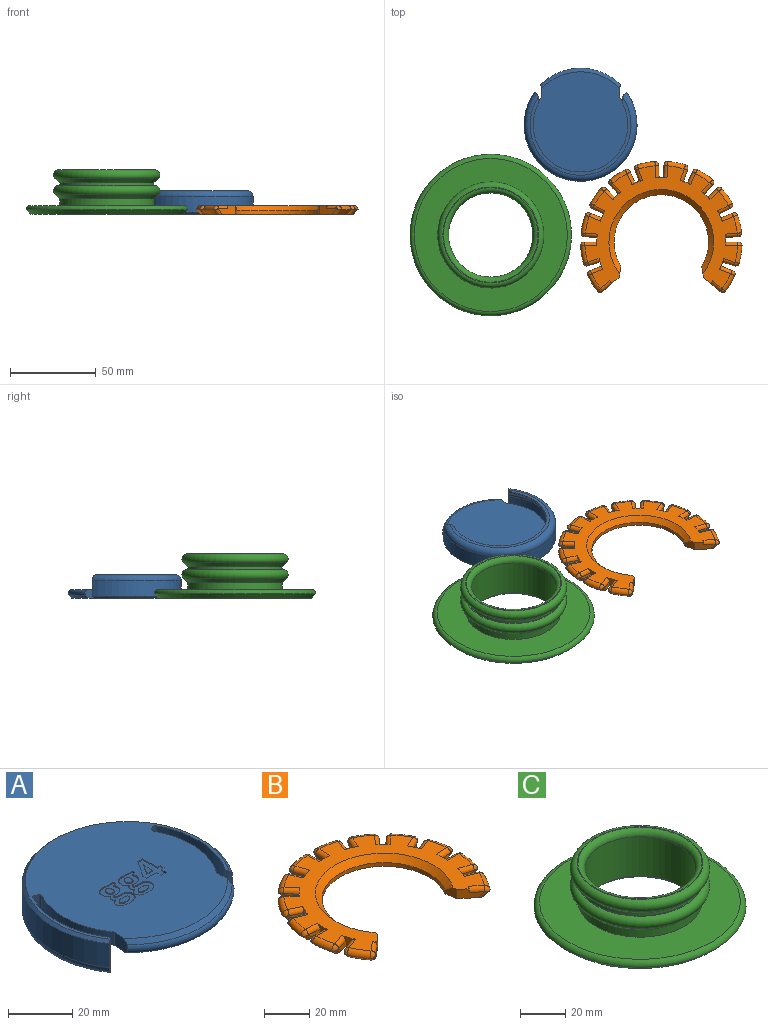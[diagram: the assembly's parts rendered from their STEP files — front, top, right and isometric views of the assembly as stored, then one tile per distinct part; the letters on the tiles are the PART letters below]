
ASSEMBLY  parts=3 mates=2
PART A: 143 faces, bbox 71.2x71.3x13.7 mm
  f0: plane 63.76x62.76mm, normal (0,0,1), area 2738mm2, adj f1,f2,f5,f6,f7,f12,f13,f17
  f1: cylinder r=27.88mm len=29.58mm, axis (0,0,-1), area 156.4mm2, adj f0,f3,f23,f28
  f2: cylinder r=27.88mm len=29.58mm, axis (0,0,-1), area 156.4mm2, adj f0,f3,f24,f26
  f3: plane 58.76x55.76mm, normal (0,0,-1), area 2597mm2, adj f1,f2,f4,f18,f23,f24
  f4: torus R=27.88mm, axis (0,0,-1), area 609.6mm2, adj f3,f5,f6,f7,f13,f14,f21,f22
  f5: plane 5.75x0.87mm, normal (-0.5,-0.87,0), area 5.4mm2, adj f0,f4,f27,f28
  f6: plane 5.75x0.87mm, normal (0.5,-0.87,0), area 5.4mm2, adj f0,f4,f25,f26
  f7: cylinder r=30.88mm len=32.12mm, axis (0,0,-1), area 270.7mm2, adj f0,f4,f22,f27
  f8: cylinder r=27.5mm len=55mm, axis (0,0,-1), area 111.5mm2, adj f9,f14,f21,f22
  f9: plane 58.76x45.55mm, normal (0,0,-1), area 226.2mm2, adj f8,f10,f21,f22
  f10: torus R=29.38mm, axis (0,0,-1), area 756.7mm2, adj f9,f11,f15,f16,f21,f22
  f11: cylinder r=32.88mm len=65.76mm, axis (0,0,-1), area 1308.5mm2, adj f10,f12,f15,f16
  f12: cone r=31.88mm half-angle=45deg, axis (0,0,-1), area 199.8mm2, adj f0,f11,f15,f16,f21,f22
  f13: cylinder r=30.88mm len=32.12mm, axis (0,0,-1), area 270.7mm2, adj f0,f4,f21,f25
  f14: cone r=27.5mm half-angle=45deg, axis (0,0,1), area 432.6mm2, adj f4,f8,f21,f22
  f15: plane 12.07x0.63mm, normal (0.57,-0.82,0), area 8.4mm2, adj f10,f11,f12,f22
  f16: plane 12.07x0.63mm, normal (-0.57,-0.82,0), area 8.4mm2, adj f10,f11,f12,f21
  f17: cone r=30.88mm half-angle=45deg, axis (0,0,-1), area 106.1mm2, adj f0,f18,f23,f24
  f18: torus R=30.88mm, axis (0,0,-1), area 250.6mm2, adj f3,f17,f19,f20,f23,f24
  f19: plane 2.59x0.32mm, normal (0.71,0.71,0), area 0.8mm2, adj f18,f24
  f20: plane 2.59x0.32mm, normal (-0.71,0.71,0), area 0.8mm2, adj f18,f23
  f21: cylinder r=5mm len=13.62mm, axis (0,0,-1), area 28.9mm2, adj f0,f4,f8,f9,f10,f12,f13,f14
  f22: cylinder r=5mm len=13.62mm, axis (0,0,-1), area 28.9mm2, adj f0,f4,f7,f8,f9,f10,f12,f14
  f23: plane 6.53x5.04mm, normal (-1,0.08,0), area 30.3mm2, adj f0,f1,f3,f17,f18,f20
  f24: plane 6.53x5.04mm, normal (1,0.08,0), area 30.3mm2, adj f0,f2,f3,f17,f18,f19
  f25: cylinder r=1mm len=8mm, axis (0,0,-1), area 10.8mm2, adj f0,f4,f6,f13
  f26: cylinder r=1mm len=5.17mm, axis (0,0,-1), area 7.8mm2, adj f0,f2,f4,f6
  f27: cylinder r=1mm len=8mm, axis (0,0,-1), area 10.8mm2, adj f0,f4,f5,f7
  f28: cylinder r=1mm len=5.17mm, axis (0,0,-1), area 7.8mm2, adj f0,f1,f4,f5
  f29: extruded ~1.03x0.4mm, area 0.4mm2, adj f30,f72,f73,f140
  f30: extruded ~1.44x1.2mm, area 0.9mm2, adj f29,f31,f73,f140
  f31: extruded ~1.44x1.18mm, area 0.9mm2, adj f30,f32,f73,f140
  f32: extruded ~1.03x0.4mm, area 0.4mm2, adj f31,f33,f73,f140
  f33: extruded ~0.9x0.4mm, area 0.4mm2, adj f32,f72,f73,f140
  f34: extruded ~0.71x0.43mm, area 0.3mm2, adj f35,f70,f73,f74
  f35: extruded ~0.74x0.4mm, area 0.4mm2, adj f34,f36,f73,f74
  f36: extruded ~1x0.4mm, area 0.4mm2, adj f35,f37,f73,f74
  f37: plane 1.13x0.4mm, normal (0,1,0), area 0.5mm2, adj f36,f38,f73,f74
  f38: extruded ~1.21x0.4mm, area 0.5mm2, adj f37,f39,f73,f74
  f39: extruded ~0.62x0.4mm, area 0.3mm2, adj f38,f40,f73,f74
  f40: extruded ~0.88x0.66mm, area 0.5mm2, adj f39,f41,f73,f74
  f41: extruded ~1.83x0.4mm, area 0.7mm2, adj f40,f70,f73,f74
  f42: plane 1.11x0.4mm, normal (-1,0,0), area 0.4mm2, adj f0,f43,f71,f73
  f43: plane 2.78x0.4mm, normal (0,-1,0), area 1.1mm2, adj f0,f42,f44,f73
  f44: extruded ~0.59x0.4mm, area 0.2mm2, adj f0,f43,f45,f73
  f45: extruded ~0.79x0.4mm, area 0.3mm2, adj f0,f44,f46,f73
  f46: extruded ~2.42x0.71mm, area 1mm2, adj f0,f45,f47,f73
  f47: extruded ~2.01x0.85mm, area 0.9mm2, adj f0,f46,f48,f73
  f48: extruded ~1.41x0.4mm, area 0.6mm2, adj f0,f47,f49,f73
  f49: extruded ~0.99x0.87mm, area 0.5mm2, adj f0,f48,f50,f73
  f50: extruded ~0.76x0.6mm, area 0.4mm2, adj f0,f49,f51,f73
  f51: extruded ~0.76x0.4mm, area 0.3mm2, adj f0,f50,f52,f73
  f52: extruded ~0.69x0.4mm, area 0.3mm2, adj f0,f51,f53,f73
  f53: extruded ~0.58x0.47mm, area 0.3mm2, adj f0,f52,f54,f73
  f54: extruded ~1.32x0.69mm, area 0.6mm2, adj f0,f53,f55,f73
  f55: extruded ~1.2x0.45mm, area 0.5mm2, adj f0,f54,f56,f73
  f56: extruded ~1.63x0.88mm, area 0.8mm2, adj f0,f55,f57,f73
  f57: extruded ~2.55x0.58mm, area 1.1mm2, adj f0,f56,f58,f73
  f58: extruded ~3.34x0.77mm, area 1.4mm2, adj f0,f57,f59,f73
  f59: extruded ~2.17x1.16mm, area 1mm2, adj f0,f58,f60,f73
  f60: extruded ~1.65x0.69mm, area 0.7mm2, adj f0,f59,f61,f73
  f61: extruded ~2x0.56mm, area 0.8mm2, adj f0,f60,f62,f73
  f62: plane 1.35x0.4mm, normal (0,-1,0), area 0.5mm2, adj f0,f61,f63,f73
  f63: extruded ~1.2x0.47mm, area 0.6mm2, adj f0,f62,f64,f73
  f64: extruded ~0.57x0.4mm, area 0.3mm2, adj f0,f63,f65,f73
  f65: plane 0.4x0.32mm, normal (0.11,0.99,0), area 0.1mm2, adj f0,f64,f66,f73
  f66: plane 0.4x0.39mm, normal (0.06,1,0), area 0.2mm2, adj f0,f65,f67,f73
  f67: extruded ~2.48x0.72mm, area 1.1mm2, adj f0,f66,f68,f73
  f68: extruded ~2x0.89mm, area 0.9mm2, adj f0,f67,f69,f73
  f69: extruded ~1.2x0.4mm, area 0.5mm2, adj f0,f68,f71,f73
  f70: extruded ~1.21x0.4mm, area 0.5mm2, adj f34,f41,f73,f74
  f71: plane 1.25x0.4mm, normal (-0.25,0.97,0), area 0.5mm2, adj f0,f42,f69,f73
  f72: extruded ~0.9x0.4mm, area 0.4mm2, adj f29,f33,f73,f140
  f73: plane 11.62x8.03mm, normal (0,0,1), area 55.2mm2, adj f29,f30,f31,f32,f33,f34,f35,f36
  f74: plane 4.13x1.99mm, normal (0,0,1), area 6.9mm2, adj f34,f35,f36,f37,f38,f39,f40,f41
  f75: extruded ~1.03x0.4mm, area 0.4mm2, adj f76,f118,f119,f141
  f76: extruded ~1.44x1.2mm, area 0.9mm2, adj f75,f77,f119,f141
  f77: extruded ~1.44x1.18mm, area 0.9mm2, adj f76,f78,f119,f141
  f78: extruded ~1.03x0.4mm, area 0.4mm2, adj f77,f79,f119,f141
  f79: extruded ~0.9x0.4mm, area 0.4mm2, adj f78,f118,f119,f141
  f80: extruded ~0.71x0.43mm, area 0.3mm2, adj f81,f116,f119,f120
  f81: extruded ~0.74x0.4mm, area 0.4mm2, adj f80,f82,f119,f120
  f82: extruded ~1x0.4mm, area 0.4mm2, adj f81,f83,f119,f120
  f83: plane 1.13x0.4mm, normal (0,1,0), area 0.5mm2, adj f82,f84,f119,f120
  f84: extruded ~1.21x0.4mm, area 0.5mm2, adj f83,f85,f119,f120
  f85: extruded ~0.62x0.4mm, area 0.3mm2, adj f84,f86,f119,f120
  f86: extruded ~0.88x0.66mm, area 0.5mm2, adj f85,f87,f119,f120
  f87: extruded ~1.83x0.4mm, area 0.7mm2, adj f86,f116,f119,f120
  f88: plane 1.11x0.4mm, normal (-1,0,0), area 0.4mm2, adj f0,f89,f117,f119
  f89: plane 2.78x0.4mm, normal (0,-1,0), area 1.1mm2, adj f0,f88,f90,f119
  f90: extruded ~0.59x0.4mm, area 0.2mm2, adj f0,f89,f91,f119
  f91: extruded ~0.79x0.4mm, area 0.3mm2, adj f0,f90,f92,f119
  f92: extruded ~2.42x0.71mm, area 1mm2, adj f0,f91,f93,f119
  f93: extruded ~2.01x0.85mm, area 0.9mm2, adj f0,f92,f94,f119
  f94: extruded ~1.41x0.4mm, area 0.6mm2, adj f0,f93,f95,f119
  f95: extruded ~0.99x0.87mm, area 0.5mm2, adj f0,f94,f96,f119
  f96: extruded ~0.76x0.6mm, area 0.4mm2, adj f0,f95,f97,f119
  f97: extruded ~0.76x0.4mm, area 0.3mm2, adj f0,f96,f98,f119
  f98: extruded ~0.69x0.4mm, area 0.3mm2, adj f0,f97,f99,f119
  f99: extruded ~0.58x0.47mm, area 0.3mm2, adj f0,f98,f100,f119
  f100: extruded ~1.32x0.69mm, area 0.6mm2, adj f0,f99,f101,f119
  f101: extruded ~1.2x0.45mm, area 0.5mm2, adj f0,f100,f102,f119
  f102: extruded ~1.63x0.88mm, area 0.8mm2, adj f0,f101,f103,f119
  f103: extruded ~2.55x0.58mm, area 1.1mm2, adj f0,f102,f104,f119
  f104: extruded ~3.34x0.77mm, area 1.4mm2, adj f0,f103,f105,f119
  f105: extruded ~2.17x1.16mm, area 1mm2, adj f0,f104,f106,f119
  f106: extruded ~1.65x0.69mm, area 0.7mm2, adj f0,f105,f107,f119
  f107: extruded ~2x0.56mm, area 0.8mm2, adj f0,f106,f108,f119
  f108: plane 1.35x0.4mm, normal (0,-1,0), area 0.5mm2, adj f0,f107,f109,f119
  f109: extruded ~1.2x0.47mm, area 0.6mm2, adj f0,f108,f110,f119
  f110: extruded ~0.57x0.4mm, area 0.3mm2, adj f0,f109,f111,f119
  f111: plane 0.4x0.32mm, normal (0.11,0.99,0), area 0.1mm2, adj f0,f110,f112,f119
  f112: plane 0.4x0.39mm, normal (0.06,1,0), area 0.2mm2, adj f0,f111,f113,f119
  f113: extruded ~2.48x0.72mm, area 1.1mm2, adj f0,f112,f114,f119
  f114: extruded ~2x0.89mm, area 0.9mm2, adj f0,f113,f115,f119
  f115: extruded ~1.2x0.4mm, area 0.5mm2, adj f0,f114,f117,f119
  f116: extruded ~1.21x0.4mm, area 0.5mm2, adj f80,f87,f119,f120
  f117: plane 1.25x0.4mm, normal (-0.25,0.97,0), area 0.5mm2, adj f0,f88,f115,f119
  f118: extruded ~0.9x0.4mm, area 0.4mm2, adj f75,f79,f119,f141
  f119: plane 11.62x8.03mm, normal (0,0,1), area 55.2mm2, adj f75,f76,f77,f78,f79,f80,f81,f82
  f120: plane 4.13x1.99mm, normal (0,0,1), area 6.9mm2, adj f80,f81,f82,f83,f84,f85,f86,f87
  f121: plane 1.77x0.4mm, normal (1,0,0), area 0.7mm2, adj f122,f138,f139,f142
  f122: plane 2.51x0.4mm, normal (0,-1,0), area 1mm2, adj f121,f123,f139,f142
  f123: plane 2.89x1.91mm, normal (-0.83,0.55,0), area 1.4mm2, adj f122,f124,f139,f142
  f124: extruded ~1.14x0.63mm, area 0.5mm2, adj f123,f125,f139,f142
  f125: plane 0.4x0.06mm, normal (0,1,0), area 0mm2, adj f124,f126,f139,f142
  f126: extruded ~0.98x0.4mm, area 0.4mm2, adj f125,f138,f139,f142
  f127: plane 1.25x0.4mm, normal (0,1,0), area 0.5mm2, adj f0,f128,f137,f139
  f128: plane 1.71x0.4mm, normal (-1,0,0), area 0.7mm2, adj f0,f127,f129,f139
  f129: plane 1.25x0.4mm, normal (0,-1,0), area 0.5mm2, adj f0,f128,f130,f139
  f130: plane 6.55x0.4mm, normal (-1,0,0), area 2.6mm2, adj f0,f129,f131,f139
  f131: plane 2.03x0.4mm, normal (0,-1,0), area 0.8mm2, adj f0,f130,f132,f139
  f132: plane 6.72x4.57mm, normal (0.83,-0.56,0), area 3.3mm2, adj f0,f131,f133,f139
  f133: plane 1.53x0.4mm, normal (1,0,0), area 0.6mm2, adj f0,f132,f134,f139
  f134: plane 4.44x0.4mm, normal (0,1,0), area 1.8mm2, adj f0,f133,f135,f139
  f135: plane 2.16x0.4mm, normal (1,0,0), area 0.9mm2, adj f0,f134,f136,f139
  f136: plane 2.15x0.4mm, normal (0,1,0), area 0.9mm2, adj f0,f135,f137,f139
  f137: plane 2.16x0.4mm, normal (-1,0,0), area 0.9mm2, adj f0,f127,f136,f139
  f138: extruded ~1.28x0.4mm, area 0.5mm2, adj f121,f126,f139,f142
  f139: plane 10.41x7.85mm, normal (0,0,1), area 41mm2, adj f121,f122,f123,f124,f125,f126,f127,f128
  f140: plane 2.84x2.38mm, normal (0,0,1), area 5.6mm2, adj f29,f30,f31,f32,f33,f72
  f141: plane 2.84x2.38mm, normal (0,0,1), area 5.6mm2, adj f75,f76,f77,f78,f79,f118
  f142: plane 4.03x2.6mm, normal (0,0,1), area 4.9mm2, adj f121,f122,f123,f124,f125,f126,f138
PART B: 139 faces, bbox 122.8x100.7x33 mm
  f0: cylinder r=37.5mm len=6.21mm, axis (0,0,-1), area 17.1mm2, adj f8,f10,f54,f61,f64,f67
  f1: cylinder r=37.5mm len=6.61mm, axis (0,0,-1), area 17.1mm2, adj f8,f10,f44,f51,f55,f58
  f2: cylinder r=37.5mm len=6.04mm, axis (0,0,-1), area 17.1mm2, adj f8,f10,f34,f41,f45,f48
  f3: cylinder r=37.5mm len=5mm, axis (0,0,-1), area 17.1mm2, adj f8,f10,f24,f31,f35,f38
  f4: cylinder r=37.5mm len=6.13mm, axis (0,0,-1), area 17.1mm2, adj f8,f10,f14,f21,f25,f28
  f5: cylinder r=37.5mm len=6.61mm, axis (0,0,-1), area 17.1mm2, adj f8,f10,f15,f18,f82,f85
  f6: cone r=27.5mm half-angle=45deg, axis (0,0,1), area 533.9mm2, adj f7,f10,f71,f138
  f7: cylinder r=27.5mm len=55mm, axis (0,0,-1), area 232.6mm2, adj f6,f8,f71,f138
  f8: plane 89.69x72.74mm, normal (0,0,-1), area 2507.1mm2, adj f0,f1,f2,f3,f4,f5,f7,f11
  f9: cylinder r=37.5mm len=2mm, axis (0,0,-1), area 2mm2, adj f10,f11,f70
  f10: plane 88.91x71.4mm, normal (0,0,1), area 1823.6mm2, adj f0,f1,f2,f3,f4,f5,f6,f9
  f11: plane 9.57x8.03mm, normal (0.64,-0.77,0), area 43.8mm2, adj f8,f9,f10,f68,f69,f70,f71
  f12: cone r=44.5mm half-angle=45deg, axis (0,0,1), area 36.2mm2, adj f8,f13,f16,f17,f19,f20
  f13: torus R=44.5mm, axis (0,0,-1), area 40.7mm2, adj f10,f12,f17,f20
  f14: plane 6.68x3mm, normal (-0.94,-0.34,0), area 16.9mm2, adj f4,f8,f19,f20,f21
  f15: plane 7.1x3mm, normal (1,0.03,0), area 16.9mm2, adj f5,f8,f16,f17,f18
  f16: bspline ~20.3x20.28mm, area 12.4mm2, adj f8,f12,f15,f17
  f17: bspline ~3.01x2.95mm, area 8.2mm2, adj f12,f13,f15,f16,f18
  f18: cylinder r=2mm len=7.07mm, axis (0.03,-1,0), area 21.9mm2, adj f5,f10,f15,f17
  f19: bspline ~24.54x23.73mm, area 12.4mm2, adj f8,f12,f14,f20
  f20: bspline ~3.39x2.95mm, area 8.2mm2, adj f12,f13,f14,f19,f21
  f21: cylinder r=2mm len=7.27mm, axis (-0.34,0.94,0), area 21.9mm2, adj f4,f10,f14,f20
  f22: cone r=44.5mm half-angle=45deg, axis (0,0,1), area 36.2mm2, adj f8,f23,f26,f27,f29,f30
  f23: torus R=44.5mm, axis (0,0,-1), area 40.7mm2, adj f10,f22,f27,f30
  f24: plane 5.28x4.75mm, normal (-0.74,-0.67,0), area 16.9mm2, adj f3,f8,f29,f30,f31
  f25: plane 6.49x3mm, normal (0.91,0.41,0), area 16.9mm2, adj f4,f8,f26,f27,f28
  f26: bspline ~20.3x18.54mm, area 12.4mm2, adj f8,f22,f25,f27
  f27: bspline ~3.5x3.07mm, area 8.2mm2, adj f22,f23,f25,f26,f28
  f28: cylinder r=2mm len=7.22mm, axis (0.41,-0.91,0), area 21.9mm2, adj f4,f10,f25,f27
  f29: bspline ~24.54x19.58mm, area 12.4mm2, adj f8,f22,f24,f30
  f30: bspline ~3.52x3.45mm, area 8.2mm2, adj f22,f23,f24,f29,f31
  f31: cylinder r=2mm len=6.55mm, axis (-0.67,0.74,0), area 21.9mm2, adj f3,f10,f24,f30
  f32: cone r=44.5mm half-angle=45deg, axis (0,0,1), area 36.2mm2, adj f8,f33,f36,f37,f39,f40
  f33: torus R=44.5mm, axis (0,0,-1), area 40.7mm2, adj f10,f32,f37,f40
  f34: plane 6.39x3.11mm, normal (-0.44,-0.9,0), area 16.9mm2, adj f2,f8,f39,f40,f41
  f35: plane 5.11x4.94mm, normal (0.69,0.72,0), area 16.9mm2, adj f3,f8,f36,f37,f38
  f36: bspline ~20.3x16mm, area 12.4mm2, adj f8,f32,f35,f37
  f37: bspline ~3.5x3.48mm, area 8.2mm2, adj f32,f33,f35,f36,f38
  f38: cylinder r=2mm len=6.43mm, axis (0.72,-0.69,0), area 21.9mm2, adj f3,f10,f35,f37
  f39: bspline ~24.54x22.06mm, area 12.4mm2, adj f8,f32,f34,f40
  f40: bspline ~3.52x3.13mm, area 8.2mm2, adj f32,f33,f34,f39,f41
  f41: cylinder r=2mm len=7.18mm, axis (-0.9,0.44,0), area 21.9mm2, adj f2,f10,f34,f40
  f42: cone r=44.5mm half-angle=45deg, axis (0,0,1), area 36.2mm2, adj f8,f43,f46,f47,f49,f50
  f43: torus R=44.5mm, axis (0,0,-1), area 40.7mm2, adj f10,f42,f47,f50
  f44: plane 7.09x3mm, normal (-0.07,-1,0), area 16.9mm2, adj f1,f8,f49,f50,f51
  f45: plane 6.59x3mm, normal (0.37,0.93,0), area 16.9mm2, adj f2,f8,f46,f47,f48
  f46: bspline ~20.3x19.55mm, area 12.4mm2, adj f8,f42,f45,f47
  f47: bspline ~3.43x2.95mm, area 8.2mm2, adj f42,f43,f45,f46,f48
  f48: cylinder r=2mm len=7.25mm, axis (0.93,-0.37,0), area 21.9mm2, adj f2,f10,f45,f47
  f49: bspline ~24.54x24.48mm, area 12.4mm2, adj f8,f42,f44,f50
  f50: bspline ~3.08x2.95mm, area 8.2mm2, adj f42,f43,f44,f49,f51
  f51: cylinder r=2mm len=7.13mm, axis (-1,0.07,0), area 21.9mm2, adj f1,f10,f44,f50
  f52: cone r=44.5mm half-angle=45deg, axis (0,0,1), area 36.2mm2, adj f8,f53,f56,f57,f59,f60
  f53: torus R=44.5mm, axis (0,0,-1), area 40.7mm2, adj f10,f52,f57,f60
  f54: plane 6.76x3mm, normal (0.31,-0.95,0), area 16.9mm2, adj f0,f8,f59,f60,f61
  f55: plane 7.1x3mm, normal (0,1,0), area 16.9mm2, adj f1,f8,f56,f57,f58
  f56: bspline ~20.3x20.3mm, area 12.4mm2, adj f8,f52,f55,f57
  f57: bspline ~2.95x2.95mm, area 8.2mm2, adj f52,f53,f55,f56,f58
  f58: cylinder r=2mm len=7.01mm, axis (1,0,0), area 21.9mm2, adj f1,f10,f55,f57
  f59: bspline ~24.54x23.94mm, area 12.4mm2, adj f8,f52,f54,f60
  f60: bspline ~3.36x2.95mm, area 8.2mm2, adj f52,f53,f54,f59,f61
  f61: cylinder r=2mm len=7.28mm, axis (-0.95,-0.31,0), area 21.9mm2, adj f0,f10,f54,f60
  f62: cone r=44.5mm half-angle=45deg, axis (0,0,1), area 36.2mm2, adj f8,f63,f65,f66,f68,f69
  f63: torus R=44.5mm, axis (0,0,-1), area 40.7mm2, adj f10,f62,f66,f69
  f64: plane 6.59x3mm, normal (-0.37,0.93,0), area 16.9mm2, adj f0,f8,f65,f66,f67
  f65: bspline ~20.3x18.82mm, area 12.4mm2, adj f8,f62,f64,f66
  f66: bspline ~3.48x3.01mm, area 8.2mm2, adj f62,f63,f64,f65,f67
  f67: cylinder r=2mm len=7.25mm, axis (0.93,0.37,0), area 21.9mm2, adj f0,f10,f64,f66
  f68: bspline ~24.54x20.09mm, area 12.4mm2, adj f8,f11,f62,f69
  f69: bspline ~3.53x3.42mm, area 8.2mm2, adj f11,f62,f63,f68,f70
  f70: cylinder r=2mm len=6.65mm, axis (-0.77,-0.64,0), area 21.9mm2, adj f9,f10,f11,f69
  f71: plane 6.62x5.21mm, normal (0.99,-0.16,0), area 25.9mm2, adj f6,f7,f8,f10,f11
  f72: cylinder r=37.5mm len=6.21mm, axis (0,0,-1), area 17.1mm2, adj f8,f10,f121,f128,f131,f134
  f73: cylinder r=37.5mm len=6.61mm, axis (0,0,-1), area 17.1mm2, adj f8,f10,f111,f118,f122,f125
  f74: cylinder r=37.5mm len=6.04mm, axis (0,0,-1), area 17.1mm2, adj f8,f10,f101,f108,f112,f115
  f75: cylinder r=37.5mm len=5mm, axis (0,0,-1), area 17.1mm2, adj f8,f10,f91,f98,f102,f105
  f76: cylinder r=37.5mm len=6.13mm, axis (0,0,-1), area 17.1mm2, adj f8,f10,f81,f88,f92,f95
  f77: cylinder r=37.5mm len=2mm, axis (0,0,-1), area 2mm2, adj f10,f78,f137
  f78: plane 9.57x8.03mm, normal (-0.64,-0.77,0), area 43.8mm2, adj f8,f10,f77,f135,f136,f137,f138
  f79: cone r=44.5mm half-angle=45deg, axis (0,0,1), area 36.2mm2, adj f8,f80,f83,f84,f86,f87
  f80: torus R=44.5mm, axis (0,0,-1), area 40.7mm2, adj f10,f79,f84,f87
  f81: plane 6.68x3mm, normal (0.94,-0.34,0), area 16.9mm2, adj f8,f76,f86,f87,f88
  f82: plane 7.1x3mm, normal (-1,0.03,0), area 16.9mm2, adj f5,f8,f83,f84,f85
  f83: bspline ~20.3x20.28mm, area 12.4mm2, adj f8,f79,f82,f84
  f84: bspline ~3.01x2.95mm, area 8.2mm2, adj f79,f80,f82,f83,f85
  f85: cylinder r=2mm len=7.07mm, axis (-0.03,-1,0), area 21.9mm2, adj f5,f10,f82,f84
  f86: bspline ~32.24x30.97mm, area 12.4mm2, adj f8,f79,f81,f87
  f87: bspline ~3.39x2.95mm, area 8.2mm2, adj f79,f80,f81,f86,f88
  f88: cylinder r=2mm len=7.27mm, axis (0.34,0.94,0), area 21.9mm2, adj f10,f76,f81,f87
  f89: cone r=44.5mm half-angle=45deg, axis (0,0,1), area 36.2mm2, adj f8,f90,f93,f94,f96,f97
  f90: torus R=44.5mm, axis (0,0,-1), area 40.7mm2, adj f10,f89,f94,f97
  f91: plane 5.28x4.75mm, normal (0.74,-0.67,0), area 16.9mm2, adj f8,f75,f96,f97,f98
  f92: plane 6.49x3mm, normal (-0.91,0.41,0), area 16.9mm2, adj f8,f76,f93,f94,f95
  f93: bspline ~20.3x18.54mm, area 12.4mm2, adj f8,f89,f92,f94
  f94: bspline ~3.5x3.07mm, area 8.2mm2, adj f89,f90,f92,f93,f95
  f95: cylinder r=2mm len=7.22mm, axis (-0.41,-0.91,0), area 21.9mm2, adj f10,f76,f92,f94
  f96: bspline ~32.24x25.31mm, area 12.4mm2, adj f8,f89,f91,f97
  f97: bspline ~3.52x3.45mm, area 8.2mm2, adj f89,f90,f91,f96,f98
  f98: cylinder r=2mm len=6.55mm, axis (0.67,0.74,0), area 21.9mm2, adj f10,f75,f91,f97
  f99: cone r=44.5mm half-angle=45deg, axis (0,0,1), area 36.2mm2, adj f8,f100,f103,f104,f106,f107
  f100: torus R=44.5mm, axis (0,0,-1), area 40.7mm2, adj f10,f99,f104,f107
  f101: plane 6.39x3.11mm, normal (0.44,-0.9,0), area 16.9mm2, adj f8,f74,f106,f107,f108
  f102: plane 5.11x4.94mm, normal (-0.69,0.72,0), area 16.9mm2, adj f8,f75,f103,f104,f105
  f103: bspline ~20.3x16mm, area 12.4mm2, adj f8,f99,f102,f104
  f104: bspline ~3.5x3.48mm, area 8.2mm2, adj f99,f100,f102,f103,f105
  f105: cylinder r=2mm len=6.43mm, axis (-0.72,-0.69,0), area 21.9mm2, adj f10,f75,f102,f104
  f106: bspline ~32.24x28.98mm, area 12.4mm2, adj f8,f99,f101,f107
  f107: bspline ~3.52x3.13mm, area 8.2mm2, adj f99,f100,f101,f106,f108
  f108: cylinder r=2mm len=7.18mm, axis (0.9,0.44,0), area 21.9mm2, adj f10,f74,f101,f107
  f109: cone r=44.5mm half-angle=45deg, axis (0,0,1), area 36.2mm2, adj f8,f110,f113,f114,f116,f117
  f110: torus R=44.5mm, axis (0,0,-1), area 40.7mm2, adj f10,f109,f114,f117
  f111: plane 7.09x3mm, normal (0.07,-1,0), area 16.9mm2, adj f8,f73,f116,f117,f118
  f112: plane 6.59x3mm, normal (-0.37,0.93,0), area 16.9mm2, adj f8,f74,f113,f114,f115
  f113: bspline ~20.3x19.55mm, area 12.4mm2, adj f8,f109,f112,f114
  f114: bspline ~3.43x2.95mm, area 8.2mm2, adj f109,f110,f112,f113,f115
  f115: cylinder r=2mm len=7.25mm, axis (-0.93,-0.37,0), area 21.9mm2, adj f10,f74,f112,f114
  f116: bspline ~32.24x32.16mm, area 12.4mm2, adj f8,f109,f111,f117
  f117: bspline ~3.08x2.95mm, area 8.2mm2, adj f109,f110,f111,f116,f118
  f118: cylinder r=2mm len=7.13mm, axis (1,0.07,0), area 21.9mm2, adj f10,f73,f111,f117
  f119: cone r=44.5mm half-angle=45deg, axis (0,0,1), area 36.2mm2, adj f8,f120,f123,f124,f126,f127
  f120: torus R=44.5mm, axis (0,0,-1), area 40.7mm2, adj f10,f119,f124,f127
  f121: plane 6.76x3mm, normal (-0.31,-0.95,0), area 16.9mm2, adj f8,f72,f126,f127,f128
  f122: plane 7.1x3mm, normal (0,1,0), area 16.9mm2, adj f8,f73,f123,f124,f125
  f123: bspline ~20.3x20.3mm, area 12.4mm2, adj f8,f119,f122,f124
  f124: bspline ~2.95x2.95mm, area 8.2mm2, adj f119,f120,f122,f123,f125
  f125: cylinder r=2mm len=7.01mm, axis (-1,0,0), area 21.9mm2, adj f10,f73,f122,f124
  f126: bspline ~32.24x31.26mm, area 12.4mm2, adj f8,f119,f121,f127
  f127: bspline ~3.36x2.95mm, area 8.2mm2, adj f119,f120,f121,f126,f128
  f128: cylinder r=2mm len=7.28mm, axis (0.95,-0.31,0), area 21.9mm2, adj f10,f72,f121,f127
  f129: cone r=44.5mm half-angle=45deg, axis (0,0,1), area 36.2mm2, adj f8,f130,f132,f133,f135,f136
  f130: torus R=44.5mm, axis (0,0,-1), area 40.7mm2, adj f10,f129,f133,f136
  f131: plane 6.59x3mm, normal (0.37,0.93,0), area 16.9mm2, adj f8,f72,f132,f133,f134
  f132: bspline ~20.3x18.82mm, area 12.4mm2, adj f8,f129,f131,f133
  f133: bspline ~3.48x3.01mm, area 8.2mm2, adj f129,f130,f131,f132,f134
  f134: cylinder r=2mm len=7.25mm, axis (-0.93,0.37,0), area 21.9mm2, adj f10,f72,f131,f133
  f135: bspline ~32.24x25.99mm, area 12.4mm2, adj f8,f78,f129,f136
  f136: bspline ~3.53x3.42mm, area 8.2mm2, adj f78,f129,f130,f135,f137
  f137: cylinder r=2mm len=6.65mm, axis (0.77,-0.64,0), area 21.9mm2, adj f10,f77,f78,f136
  f138: plane 6.62x5.21mm, normal (-0.99,-0.16,0), area 25.9mm2, adj f6,f7,f8,f10,f78
PART C: 15 faces, bbox 101.7x101.7x25.7 mm
  f0: cylinder r=27.5mm len=55mm, axis (0,0,-1), area 259.2mm2, adj f1,f14
  f1: cone r=27.5mm half-angle=45deg, axis (0,0,1), area 638.7mm2, adj f0,f2
  f2: torus R=27.88mm, axis (0,0,-1), area 1334.7mm2, adj f1,f3
  f3: plane 55.76x55.76mm, normal (0,0,1), area 65.9mm2, adj f2,f4
  f4: torus R=27.5mm, axis (0,0,-1), area 757.7mm2, adj f3,f5
  f5: cylinder r=24.5mm len=49mm, axis (0,0,-1), area 3283.3mm2, adj f4,f6
  f6: cone r=24.5mm half-angle=45deg, axis (0,0,-1), area 316.8mm2, adj f5,f7
  f7: plane 89x89mm, normal (0,0,-1), area 4111.4mm2, adj f6,f8
  f8: cone r=44.5mm half-angle=45deg, axis (0,0,1), area 1016.3mm2, adj f7,f9
  f9: torus R=44.5mm, axis (0,0,-1), area 1137.3mm2, adj f8,f10
  f10: plane 89x89mm, normal (0,0,1), area 3845.3mm2, adj f9,f11
  f11: cylinder r=27.5mm len=55mm, axis (0,0,-1), area 691.2mm2, adj f10,f12
  f12: cone r=27.5mm half-angle=45deg, axis (0,0,1), area 638.7mm2, adj f11,f13
  f13: torus R=27.88mm, axis (0,0,-1), area 1334.7mm2, adj f12,f14
  f14: plane 55.76x55.76mm, normal (0,0,1), area 65.9mm2, adj f0,f13
PLACE A rot(axis=(1,0,0),180deg) t=(52.24,64.1,30.74)mm
PLACE B t=(99.22,-4.06,-7)mm
PLACE C at identity fixed
MATE planar A.f140 <-> C.f0  axis (0,0,-1) through (52.26,63.17,0)mm
MATE planar C.f0 <-> B.f0  axis (0,0,-1) through (0,0,0)mm
